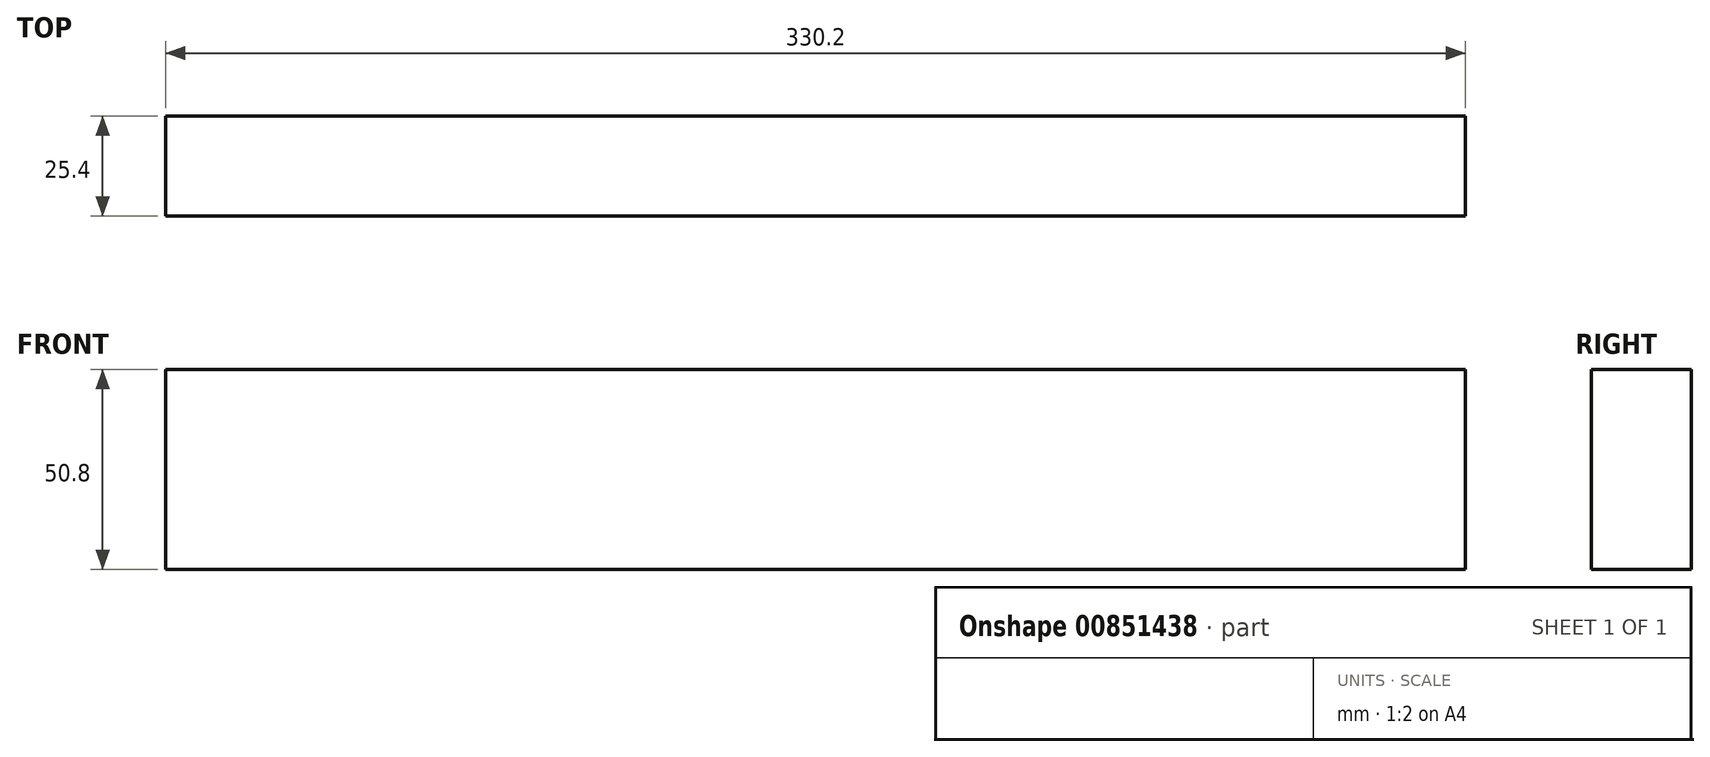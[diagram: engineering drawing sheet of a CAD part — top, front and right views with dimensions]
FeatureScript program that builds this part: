
annotation { "Feature Type Name" : "Feature", "Feature Type Description" : "" }
export const myFeature = defineFeature(function(context is Context, id is Id, definition is map)
    precondition{}
    {
        {
            var Q0;
            Q0=qCreatedBy(makeId("Front.planeOp"),FACE);
            var sketch = newSketch(context, id + "F0", { "sketchPlane" : qUnion([Q0])});
            skLineSegment(sketch, "E0", {"start": v(0, 0) * mm, "end": v(330.2, 0) * mm});
            skLineSegment(sketch, "E1", {"start": v(330.2, 0) * mm, "end": v(330.2, 50.8) * mm});
            skLineSegment(sketch, "E2", {"start": v(330.2, 50.8) * mm, "end": v(0, 50.8) * mm});
            skLineSegment(sketch, "E3", {"start": v(0, 50.8) * mm, "end": v(0, 0) * mm});
            skSolve(sketch);
        }
        {
            var Q0;
            Q0 = qSketchRegion(id + "F0", true);
            extrude(context, id + "F1", {"entities" : qUnion([Q0]), "depth" : 25.4 * mm, "offsetDistance" : 25.4 * mm});
        }
    });
